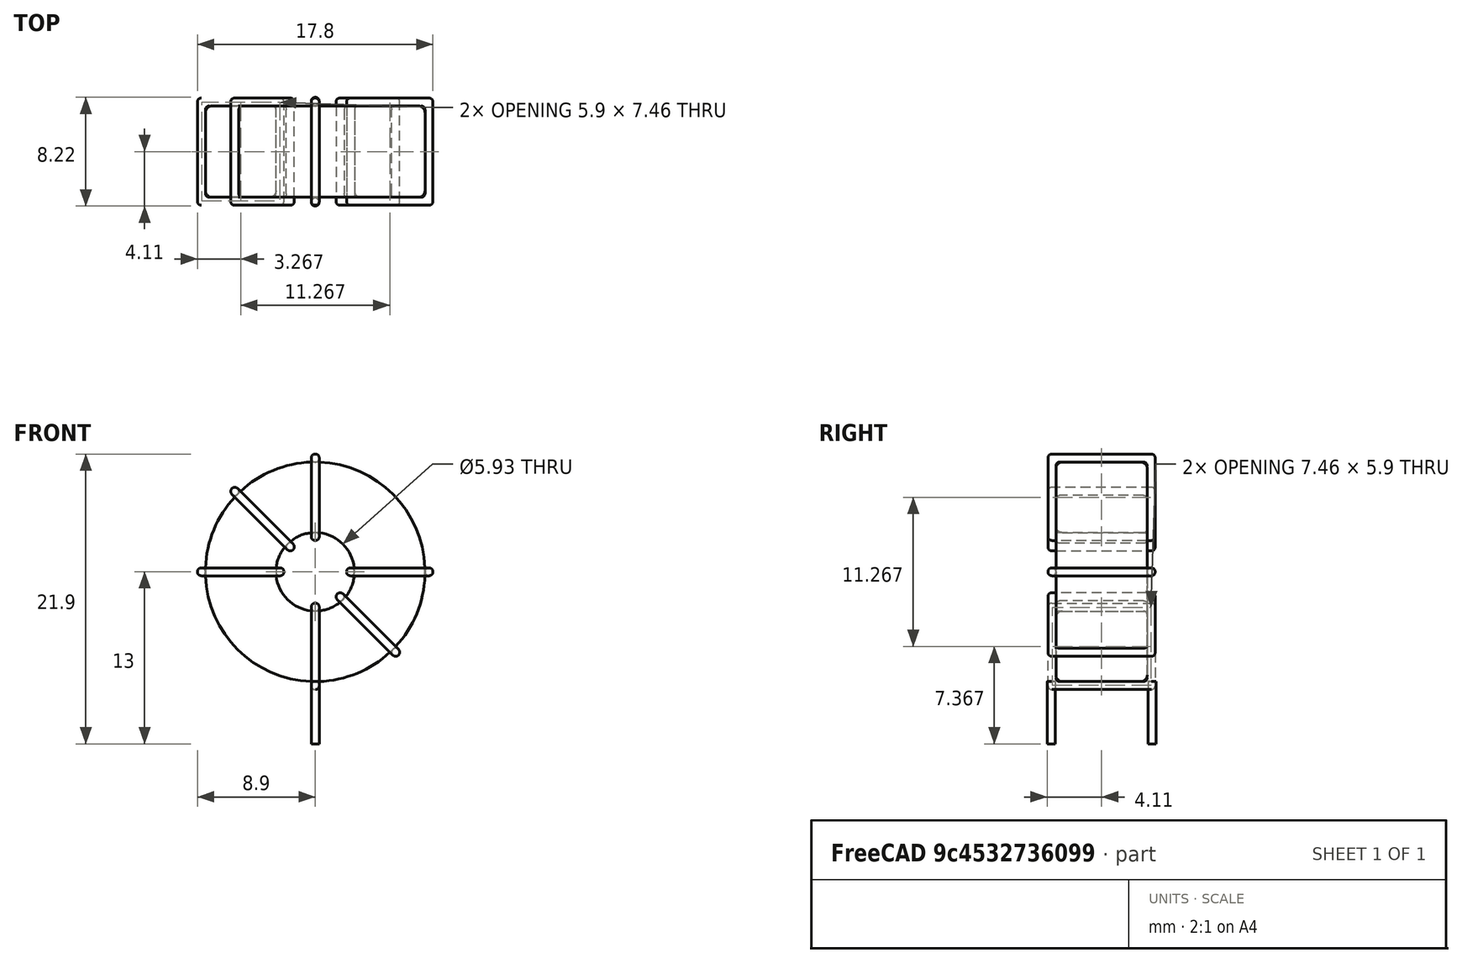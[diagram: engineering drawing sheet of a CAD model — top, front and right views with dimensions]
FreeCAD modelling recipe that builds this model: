
FCSTD DOCUMENT  (FreeCAD 0.16R6703 (Git))
Label: L_Toroid_Vertical_L17.8mm_W8.1mm_P7.62mm_Bourns_5700series
License: All rights reserved
LicenseURL: http://en.wikipedia.org/wiki/All_rights_reserved
objects: Sketcher::SketchObject×6, PartDesign::Pad×6, PartDesign::Fillet×5, Spreadsheet::Sheet×1
note: 23 computed .brp shape members not serialized (recipe doc carries the construction recipe); baked Part::Feature solids carry a one-line shape summary decoded from their .brp

FEATURE [Spreadsheet::Sheet] Spreadsheet  label="dimensions"
  cells = A1=Wx; B1(Wx)=17.8; C1(WW)=5.933333333333334; D1=17.8; A2=Wy; B2(Wy)=8.1; D2=8.1; A3=RM; B3(RMx)=7.62; C3(RMy)=0; A4=d_wire; B4(d_wire)=0.6000000000000001; A5=H; B5(H)=17.8; A6=offsetx; B6(offsetx)=8.9
FEATURE [Sketcher::SketchObject] Sketch
  Placement = pos=(0,-3.81,0) rot=(1,0,0;1.5708rad)
  expr: Placement.Base.y = -Spreadsheet.RMx / 2
  expr: Constraints[0] = Spreadsheet.Wx / 2 - Spreadsheet.d_wire
  expr: Constraints[4] = Spreadsheet.WW / 2
  expr: Constraints[2] = Spreadsheet.Wx / 2 + Spreadsheet.d_wire + 0.5
  sketch-geometry (2):
    g0: Circle CenterX=0 CenterY=10 CenterZ=0 NormalX=0 NormalY=0 NormalZ=1 Radius=8.3
    g1: Circle CenterX=0 CenterY=10 CenterZ=0 NormalX=0 NormalY=0 NormalZ=1 Radius=2.96667
  constraints (5):
    c: Radius(g0) = 8.3
    c: DistanceX(g-1,g0) = 0
    c: DistanceY(g-1,g0) = 10
    c: Coincident(g1,g0)
    c: Radius(g1) = 2.96667
FEATURE [PartDesign::Pad] Pad
  Length = 6.9
  Length2 = 100
  Midplane = true
  Placement = pos=(0,-3.81,0) rot=(1,0,0;1.5708rad)
  Sketch = -> Sketch
  Type = 0
  expr: Length = Spreadsheet.Wy - 2 * Spreadsheet.d_wire
FEATURE [Sketcher::SketchObject] Sketch001
  Placement = pos=(0,0,1.1) rot=(0,0,1;0rad)
  expr: Placement.Base.z = 0.5 + Spreadsheet.d_wire
  expr: Constraints[4] = Spreadsheet.RMy
  expr: Constraints[2] = -Spreadsheet.RMx
  expr: Constraints[1] = Spreadsheet.d_wire / 2
  sketch-geometry (2):
    g0: Circle CenterX=0 CenterY=0 CenterZ=0 NormalX=0 NormalY=0 NormalZ=1 Radius=0.3
    g1: Circle CenterX=0 CenterY=-7.62 CenterZ=0 NormalX=0 NormalY=0 NormalZ=1 Radius=0.3
  constraints (5):
    c: Equal(g0,g1)
    c: Radius(g0) = 0.3
    c: DistanceY(g-1,g1) = -7.62
    c: Coincident(g0,g-1)
    c: DistanceX(g-1,g1) = 0
FEATURE [PartDesign::Pad] Pad001
  Length = 0.6
  Length2 = 4.1
  Placement = pos=(0,0,1.1) rot=(0,0,1;0rad)
  Reversed = true
  Sketch = -> Sketch001
  Type = 4
  expr: Length2 = 3.5 + Spreadsheet.d_wire
  expr: Length = Spreadsheet.d_wire
FEATURE [PartDesign::Fillet] Fillet
  Base = -> Pad [Edge6,Edge3,Edge2]
  Placement = pos=(0,-3.81,0) rot=(1,0,0;1.5708rad)
  Radius = 0.5
FEATURE [Sketcher::SketchObject] Sketch003
  Placement = pos=(0,0.24,10) rot=(1,0,0;3.14159rad)
  expr: Constraints[18] = Spreadsheet.d_wire
  expr: Constraints[16] = Spreadsheet.d_wire
  expr: Constraints[19] = Spreadsheet.d_wire
  expr: Constraints[17] = Spreadsheet.d_wire
  expr: Placement.Base.y = -1 * (Spreadsheet.RMx - Spreadsheet.Wy) / 2
  expr: Constraints[21] = (Spreadsheet.Wx - Spreadsheet.WW) / 2 - Spreadsheet.d_wire
  expr: Constraints[22] = Spreadsheet.Wx / 2 - Spreadsheet.d_wire
  expr: Constraints[43] = Spreadsheet.d_wire
  expr: Constraints[48] = Spreadsheet.Wx - Spreadsheet.d_wire * 2
  expr: Constraints[49] = Spreadsheet.Wy
  expr: Placement.Base.z = Spreadsheet.Wx / 2 + Spreadsheet.d_wire + 0.5
  sketch-geometry (16):
    g0: LineSegment StartX=-2.36667 StartY=0 StartZ=0 EndX=-8.9 EndY=0 EndZ=0
    g1: LineSegment StartX=-8.9 StartY=0 StartZ=0 EndX=-8.9 EndY=8.1 EndZ=0
    g2: LineSegment StartX=-8.9 StartY=8.1 StartZ=0 EndX=-2.36667 EndY=8.1 EndZ=0
    g3: LineSegment StartX=-2.36667 StartY=8.1 StartZ=0 EndX=-2.36667 EndY=0 EndZ=0
    g4: LineSegment StartX=-8.3 StartY=7.5 StartZ=0 EndX=-2.96667 EndY=7.5 EndZ=0
    g5: LineSegment StartX=-2.96667 StartY=7.5 StartZ=0 EndX=-2.96667 EndY=0.6 EndZ=0
    g6: LineSegment StartX=-2.96667 StartY=0.6 StartZ=0 EndX=-8.3 EndY=0.6 EndZ=0
    g7: LineSegment StartX=-8.3 StartY=0.6 StartZ=0 EndX=-8.3 EndY=7.5 EndZ=0
    g8: LineSegment StartX=2.36667 StartY=8.1 StartZ=0 EndX=8.9 EndY=8.1 EndZ=0
    g9: LineSegment StartX=8.9 StartY=8.1 StartZ=0 EndX=8.9 EndY=0 EndZ=0
    g10: LineSegment StartX=8.9 StartY=0 StartZ=0 EndX=2.36667 EndY=0 EndZ=0
    g11: LineSegment StartX=2.36667 StartY=0 StartZ=0 EndX=2.36667 EndY=8.1 EndZ=0
    g12: LineSegment StartX=2.96667 StartY=7.5 StartZ=0 EndX=8.3 EndY=7.5 EndZ=0
    g13: LineSegment StartX=8.3 StartY=7.5 StartZ=0 EndX=8.3 EndY=0.6 EndZ=0
    g14: LineSegment StartX=8.3 StartY=0.6 StartZ=0 EndX=2.96667 EndY=0.6 EndZ=0
    g15: LineSegment StartX=2.96667 StartY=0.6 StartZ=0 EndX=2.96667 EndY=7.5 EndZ=0
  constraints (50):
    c: Horizontal(g0)
    c: Coincident(g1,g0)
    c: Vertical(g1)
    c: Coincident(g2,g1)
    c: Horizontal(g2)
    c: Coincident(g3,g2)
    c: Coincident(g3,g0)
    c: Vertical(g3)
    c: Coincident(g4,g5)
    c: Coincident(g5,g6)
    c: Coincident(g6,g7)
    c: Coincident(g7,g4)
    c: Horizontal(g4)
    c: Horizontal(g6)
    c: Vertical(g5)
    c: Vertical(g7)
    c: DistanceX(g1,g4) = 0.6
    c: DistanceY(g4,g1) = 0.6
    c: DistanceX(g5,g0) = 0.6
    c: DistanceY(g0,g5) = 0.6
    c: DistanceY(g-1,g0) = 0
    c: DistanceX(g6,g6) = 5.33333
    c: DistanceX(g6,g-1) = 8.3
    c: Coincident(g8,g9)
    c: Coincident(g9,g10)
    c: Coincident(g10,g11)
    c: Coincident(g11,g8)
    c: Horizontal(g8)
    c: Horizontal(g10)
    c: Vertical(g9)
    c: Vertical(g11)
    c: Coincident(g12,g13)
    c: Coincident(g13,g14)
    c: Coincident(g14,g15)
    c: Coincident(g15,g12)
    c: Horizontal(g12)
    c: Horizontal(g14)
    c: Vertical(g13)
    c: Vertical(g15)
    c: DistanceY(g8,g2) = 0
    c: DistanceY(g10,g0) = 0
    c: DistanceY(g14,g5) = 0
    c: DistanceY(g12,g4) = 0
    c: DistanceX(g8,g12) = 0.6
    c: Equal(g8,g2)
    c: Equal(g12,g4)
    c: Equal(g9,g1)
    c: Equal(g13,g7)
    c: DistanceX(g4,g12) = 16.6
    c: DistanceY(g0,g1) = 8.1
FEATURE [PartDesign::Pad] Pad002
  Length = 0.6
  Length2 = 100
  Midplane = true
  Placement = pos=(0,0.24,10) rot=(1,0,0;3.14159rad)
  Sketch = -> Sketch003
  Type = 0
  expr: Length = Spreadsheet.d_wire
FEATURE [PartDesign::Fillet] Fillet001
  Base = -> Pad002 [Edge38,Edge41,Edge42,Edge43,Edge29,Edge32,Edge33,Edge34,Edge25,Edge35,Edge36,Edge13,Edge14,Edge15,Edge16,Edge17,Edge18,Edge19,Edge1,Edge2,Edge3,Edge4,Edge5,Edge6,Edge7,Edge37,Edge39,Edge40,Edge20,Edge23,Edge24,Edge21,Edge22,Edge8,Edge9,Edge10,Edge11,Edge12,Edge26,Edge27,+8 more]
  Placement = pos=(0,0.24,10) rot=(1,0,0;3.14159rad)
  Radius = 0.282
  expr: Radius = Spreadsheet.d_wire * 0.47
FEATURE [Sketcher::SketchObject] Sketch004
  Placement = pos=(0,0.24,10) rot=(0.92388,0,0.382683;3.14159rad)
  expr: Constraints[18] = Spreadsheet.d_wire
  expr: Constraints[16] = Spreadsheet.d_wire
  expr: Constraints[19] = Spreadsheet.d_wire
  expr: Constraints[17] = Spreadsheet.d_wire
  expr: Placement.Base.y = -1 * (Spreadsheet.RMx - Spreadsheet.Wy) / 2
  expr: Constraints[21] = (Spreadsheet.Wx - Spreadsheet.WW) / 2 - Spreadsheet.d_wire
  expr: Constraints[22] = Spreadsheet.Wx / 2 - Spreadsheet.d_wire
  expr: Constraints[43] = Spreadsheet.d_wire
  expr: Constraints[48] = Spreadsheet.Wx - 2 * Spreadsheet.d_wire
  expr: Constraints[49] = Spreadsheet.Wy
  expr: Placement.Base.z = Spreadsheet.Wx / 2 + Spreadsheet.d_wire + 0.5
  sketch-geometry (16):
    g0: LineSegment StartX=-2.36667 StartY=0 StartZ=0 EndX=-8.9 EndY=0 EndZ=0
    g1: LineSegment StartX=-8.9 StartY=0 StartZ=0 EndX=-8.9 EndY=8.1 EndZ=0
    g2: LineSegment StartX=-8.9 StartY=8.1 StartZ=0 EndX=-2.36667 EndY=8.1 EndZ=0
    g3: LineSegment StartX=-2.36667 StartY=8.1 StartZ=0 EndX=-2.36667 EndY=0 EndZ=0
    g4: LineSegment StartX=-8.3 StartY=7.5 StartZ=0 EndX=-2.96667 EndY=7.5 EndZ=0
    g5: LineSegment StartX=-2.96667 StartY=7.5 StartZ=0 EndX=-2.96667 EndY=0.6 EndZ=0
    g6: LineSegment StartX=-2.96667 StartY=0.6 StartZ=0 EndX=-8.3 EndY=0.6 EndZ=0
    g7: LineSegment StartX=-8.3 StartY=0.6 StartZ=0 EndX=-8.3 EndY=7.5 EndZ=0
    g8: LineSegment StartX=2.36667 StartY=8.1 StartZ=0 EndX=8.9 EndY=8.1 EndZ=0
    g9: LineSegment StartX=8.9 StartY=8.1 StartZ=0 EndX=8.9 EndY=0 EndZ=0
    g10: LineSegment StartX=8.9 StartY=0 StartZ=0 EndX=2.36667 EndY=0 EndZ=0
    g11: LineSegment StartX=2.36667 StartY=0 StartZ=0 EndX=2.36667 EndY=8.1 EndZ=0
    g12: LineSegment StartX=2.96667 StartY=7.5 StartZ=0 EndX=8.3 EndY=7.5 EndZ=0
    g13: LineSegment StartX=8.3 StartY=7.5 StartZ=0 EndX=8.3 EndY=0.6 EndZ=0
    g14: LineSegment StartX=8.3 StartY=0.6 StartZ=0 EndX=2.96667 EndY=0.6 EndZ=0
    g15: LineSegment StartX=2.96667 StartY=0.6 StartZ=0 EndX=2.96667 EndY=7.5 EndZ=0
  constraints (50):
    c: Horizontal(g0)
    c: Coincident(g1,g0)
    c: Vertical(g1)
    c: Coincident(g2,g1)
    c: Horizontal(g2)
    c: Coincident(g3,g2)
    c: Coincident(g3,g0)
    c: Vertical(g3)
    c: Coincident(g4,g5)
    c: Coincident(g5,g6)
    c: Coincident(g6,g7)
    c: Coincident(g7,g4)
    c: Horizontal(g4)
    c: Horizontal(g6)
    c: Vertical(g5)
    c: Vertical(g7)
    c: DistanceX(g1,g4) = 0.6
    c: DistanceY(g4,g1) = 0.6
    c: DistanceX(g5,g0) = 0.6
    c: DistanceY(g0,g5) = 0.6
    c: DistanceY(g-1,g0) = 0
    c: DistanceX(g6,g6) = 5.33333
    c: DistanceX(g6,g-1) = 8.3
    c: Coincident(g8,g9)
    c: Coincident(g9,g10)
    c: Coincident(g10,g11)
    c: Coincident(g11,g8)
    c: Horizontal(g8)
    c: Horizontal(g10)
    c: Vertical(g9)
    c: Vertical(g11)
    c: Coincident(g12,g13)
    c: Coincident(g13,g14)
    c: Coincident(g14,g15)
    c: Coincident(g15,g12)
    c: Horizontal(g12)
    c: Horizontal(g14)
    c: Vertical(g13)
    c: Vertical(g15)
    c: DistanceY(g8,g2) = 0
    c: DistanceY(g10,g0) = 0
    c: DistanceY(g14,g5) = 0
    c: DistanceY(g12,g4) = 0
    c: DistanceX(g8,g12) = 0.6
    c: Equal(g8,g2)
    c: Equal(g12,g4)
    c: Equal(g9,g1)
    c: Equal(g13,g7)
    c: DistanceX(g4,g12) = 16.6
    c: DistanceY(g0,g1) = 8.1
FEATURE [PartDesign::Pad] Pad003
  Length = 0.6
  Length2 = 100
  Midplane = true
  Placement = pos=(0,0.24,10) rot=(0.92388,0,0.382683;3.14159rad)
  Sketch = -> Sketch004
  Type = 0
  expr: Length = Spreadsheet.d_wire
FEATURE [PartDesign::Fillet] Fillet002
  Base = -> Pad003 [Edge38,Edge41,Edge42,Edge43,Edge29,Edge32,Edge33,Edge34,Edge25,Edge35,Edge36,Edge13,Edge14,Edge15,Edge16,Edge17,Edge18,Edge19,Edge1,Edge2,Edge3,Edge4,Edge5,Edge6,Edge7,Edge37,Edge39,Edge40,Edge20,Edge23,Edge24,Edge21,Edge22,Edge8,Edge9,Edge10,Edge11,Edge12,Edge26,Edge27,+8 more]
  Placement = pos=(0,0.24,10) rot=(0.92388,0,0.382683;3.14159rad)
  Radius = 0.282
  expr: Radius = Spreadsheet.d_wire * 0.47
FEATURE [Sketcher::SketchObject] Sketch005
  Placement = pos=(0,0.24,10) rot=(0.92388,0,-0.382683;3.14159rad)
  expr: Constraints[18] = Spreadsheet.d_wire
  expr: Constraints[16] = Spreadsheet.d_wire
  expr: Constraints[19] = Spreadsheet.d_wire
  expr: Constraints[17] = Spreadsheet.d_wire
  expr: Placement.Base.y = -1 * (Spreadsheet.RMx - Spreadsheet.Wy) / 2
  expr: Constraints[21] = (Spreadsheet.Wx - Spreadsheet.WW) / 2 - Spreadsheet.d_wire
  expr: Constraints[22] = Spreadsheet.Wx / 2 - Spreadsheet.d_wire
  expr: Constraints[43] = Spreadsheet.d_wire
  expr: Constraints[48] = Spreadsheet.Wx - 2 * Spreadsheet.d_wire
  expr: Constraints[49] = Spreadsheet.Wy
  expr: Placement.Base.z = Spreadsheet.Wx / 2 + Spreadsheet.d_wire + 0.5
  sketch-geometry (16):
    g0: LineSegment StartX=-2.36667 StartY=0 StartZ=0 EndX=-8.9 EndY=0 EndZ=0
    g1: LineSegment StartX=-8.9 StartY=0 StartZ=0 EndX=-8.9 EndY=8.1 EndZ=0
    g2: LineSegment StartX=-8.9 StartY=8.1 StartZ=0 EndX=-2.36667 EndY=8.1 EndZ=0
    g3: LineSegment StartX=-2.36667 StartY=8.1 StartZ=0 EndX=-2.36667 EndY=0 EndZ=0
    g4: LineSegment StartX=-8.3 StartY=7.5 StartZ=0 EndX=-2.96667 EndY=7.5 EndZ=0
    g5: LineSegment StartX=-2.96667 StartY=7.5 StartZ=0 EndX=-2.96667 EndY=0.6 EndZ=0
    g6: LineSegment StartX=-2.96667 StartY=0.6 StartZ=0 EndX=-8.3 EndY=0.6 EndZ=0
    g7: LineSegment StartX=-8.3 StartY=0.6 StartZ=0 EndX=-8.3 EndY=7.5 EndZ=0
    g8: LineSegment StartX=2.36667 StartY=8.1 StartZ=0 EndX=8.9 EndY=8.1 EndZ=0
    g9: LineSegment StartX=8.9 StartY=8.1 StartZ=0 EndX=8.9 EndY=0 EndZ=0
    g10: LineSegment StartX=8.9 StartY=0 StartZ=0 EndX=2.36667 EndY=0 EndZ=0
    g11: LineSegment StartX=2.36667 StartY=0 StartZ=0 EndX=2.36667 EndY=8.1 EndZ=0
    g12: LineSegment StartX=2.96667 StartY=7.5 StartZ=0 EndX=8.3 EndY=7.5 EndZ=0
    g13: LineSegment StartX=8.3 StartY=7.5 StartZ=0 EndX=8.3 EndY=0.6 EndZ=0
    g14: LineSegment StartX=8.3 StartY=0.6 StartZ=0 EndX=2.96667 EndY=0.6 EndZ=0
    g15: LineSegment StartX=2.96667 StartY=0.6 StartZ=0 EndX=2.96667 EndY=7.5 EndZ=0
  constraints (50):
    c: Horizontal(g0)
    c: Coincident(g1,g0)
    c: Vertical(g1)
    c: Coincident(g2,g1)
    c: Horizontal(g2)
    c: Coincident(g3,g2)
    c: Coincident(g3,g0)
    c: Vertical(g3)
    c: Coincident(g4,g5)
    c: Coincident(g5,g6)
    c: Coincident(g6,g7)
    c: Coincident(g7,g4)
    c: Horizontal(g4)
    c: Horizontal(g6)
    c: Vertical(g5)
    c: Vertical(g7)
    c: DistanceX(g1,g4) = 0.6
    c: DistanceY(g4,g1) = 0.6
    c: DistanceX(g5,g0) = 0.6
    c: DistanceY(g0,g5) = 0.6
    c: DistanceY(g-1,g0) = 0
    c: DistanceX(g6,g6) = 5.33333
    c: DistanceX(g6,g-1) = 8.3
    c: Coincident(g8,g9)
    c: Coincident(g9,g10)
    c: Coincident(g10,g11)
    c: Coincident(g11,g8)
    c: Horizontal(g8)
    c: Horizontal(g10)
    c: Vertical(g9)
    c: Vertical(g11)
    c: Coincident(g12,g13)
    c: Coincident(g13,g14)
    c: Coincident(g14,g15)
    c: Coincident(g15,g12)
    c: Horizontal(g12)
    c: Horizontal(g14)
    c: Vertical(g13)
    c: Vertical(g15)
    c: DistanceY(g8,g2) = 0
    c: DistanceY(g10,g0) = 0
    c: DistanceY(g14,g5) = 0
    c: DistanceY(g12,g4) = 0
    c: DistanceX(g8,g12) = 0.6
    c: Equal(g8,g2)
    c: Equal(g12,g4)
    c: Equal(g9,g1)
    c: Equal(g13,g7)
    c: DistanceX(g4,g12) = 16.6
    c: DistanceY(g0,g1) = 8.1
FEATURE [PartDesign::Pad] Pad004
  Length = 0.6
  Length2 = 100
  Midplane = true
  Placement = pos=(0,0.24,10) rot=(0.92388,0,-0.382683;3.14159rad)
  Sketch = -> Sketch005
  Type = 0
  expr: Length = Spreadsheet.d_wire
FEATURE [PartDesign::Fillet] Fillet003
  Base = -> Pad004 [Edge38,Edge41,Edge42,Edge43,Edge29,Edge32,Edge33,Edge34,Edge25,Edge35,Edge36,Edge13,Edge14,Edge15,Edge16,Edge17,Edge18,Edge19,Edge1,Edge2,Edge3,Edge4,Edge5,Edge6,Edge7,Edge37,Edge39,Edge40,Edge20,Edge23,Edge24,Edge21,Edge22,Edge8,Edge9,Edge10,Edge11,Edge12,Edge26,Edge27,+8 more]
  Placement = pos=(0,0.24,10) rot=(0.92388,0,-0.382683;3.14159rad)
  Radius = 0.282
  expr: Radius = Spreadsheet.d_wire * 0.47
FEATURE [Sketcher::SketchObject] Sketch006
  Placement = pos=(0,0.24,10) rot=(0.707107,0,0.707107;3.14159rad)
  expr: Constraints[18] = Spreadsheet.d_wire
  expr: Constraints[16] = Spreadsheet.d_wire
  expr: Constraints[19] = Spreadsheet.d_wire
  expr: Constraints[17] = Spreadsheet.d_wire
  expr: Placement.Base.y = -1 * (Spreadsheet.RMx - Spreadsheet.Wy) / 2
  expr: Constraints[21] = (Spreadsheet.Wx - Spreadsheet.WW) / 2 - Spreadsheet.d_wire
  expr: Constraints[22] = Spreadsheet.Wx / 2 - Spreadsheet.d_wire
  expr: Constraints[43] = Spreadsheet.d_wire
  expr: Constraints[48] = Spreadsheet.Wx - Spreadsheet.d_wire * 2
  expr: Constraints[49] = Spreadsheet.Wy
  expr: Placement.Base.z = Spreadsheet.Wx / 2 + Spreadsheet.d_wire + 0.5
  sketch-geometry (16):
    g0: LineSegment StartX=-2.36667 StartY=0 StartZ=0 EndX=-8.9 EndY=0 EndZ=0
    g1: LineSegment StartX=-8.9 StartY=0 StartZ=0 EndX=-8.9 EndY=8.1 EndZ=0
    g2: LineSegment StartX=-8.9 StartY=8.1 StartZ=0 EndX=-2.36667 EndY=8.1 EndZ=0
    g3: LineSegment StartX=-2.36667 StartY=8.1 StartZ=0 EndX=-2.36667 EndY=0 EndZ=0
    g4: LineSegment StartX=-8.3 StartY=7.5 StartZ=0 EndX=-2.96667 EndY=7.5 EndZ=0
    g5: LineSegment StartX=-2.96667 StartY=7.5 StartZ=0 EndX=-2.96667 EndY=0.6 EndZ=0
    g6: LineSegment StartX=-2.96667 StartY=0.6 StartZ=0 EndX=-8.3 EndY=0.6 EndZ=0
    g7: LineSegment StartX=-8.3 StartY=0.6 StartZ=0 EndX=-8.3 EndY=7.5 EndZ=0
    g8: LineSegment StartX=2.36667 StartY=8.1 StartZ=0 EndX=8.9 EndY=8.1 EndZ=0
    g9: LineSegment StartX=8.9 StartY=8.1 StartZ=0 EndX=8.9 EndY=0 EndZ=0
    g10: LineSegment StartX=8.9 StartY=0 StartZ=0 EndX=2.36667 EndY=0 EndZ=0
    g11: LineSegment StartX=2.36667 StartY=0 StartZ=0 EndX=2.36667 EndY=8.1 EndZ=0
    g12: LineSegment StartX=2.96667 StartY=7.5 StartZ=0 EndX=8.3 EndY=7.5 EndZ=0
    g13: LineSegment StartX=8.3 StartY=7.5 StartZ=0 EndX=8.3 EndY=0.6 EndZ=0
    g14: LineSegment StartX=8.3 StartY=0.6 StartZ=0 EndX=2.96667 EndY=0.6 EndZ=0
    g15: LineSegment StartX=2.96667 StartY=0.6 StartZ=0 EndX=2.96667 EndY=7.5 EndZ=0
  constraints (50):
    c: Horizontal(g0)
    c: Coincident(g1,g0)
    c: Vertical(g1)
    c: Coincident(g2,g1)
    c: Horizontal(g2)
    c: Coincident(g3,g2)
    c: Coincident(g3,g0)
    c: Vertical(g3)
    c: Coincident(g4,g5)
    c: Coincident(g5,g6)
    c: Coincident(g6,g7)
    c: Coincident(g7,g4)
    c: Horizontal(g4)
    c: Horizontal(g6)
    c: Vertical(g5)
    c: Vertical(g7)
    c: DistanceX(g1,g4) = 0.6
    c: DistanceY(g4,g1) = 0.6
    c: DistanceX(g5,g0) = 0.6
    c: DistanceY(g0,g5) = 0.6
    c: DistanceY(g-1,g0) = 0
    c: DistanceX(g6,g6) = 5.33333
    c: DistanceX(g6,g-1) = 8.3
    c: Coincident(g8,g9)
    c: Coincident(g9,g10)
    c: Coincident(g10,g11)
    c: Coincident(g11,g8)
    c: Horizontal(g8)
    c: Horizontal(g10)
    c: Vertical(g9)
    c: Vertical(g11)
    c: Coincident(g12,g13)
    c: Coincident(g13,g14)
    c: Coincident(g14,g15)
    c: Coincident(g15,g12)
    c: Horizontal(g12)
    c: Horizontal(g14)
    c: Vertical(g13)
    c: Vertical(g15)
    c: DistanceY(g8,g2) = 0
    c: DistanceY(g10,g0) = 0
    c: DistanceY(g14,g5) = 0
    c: DistanceY(g12,g4) = 0
    c: DistanceX(g8,g12) = 0.6
    c: Equal(g8,g2)
    c: Equal(g12,g4)
    c: Equal(g9,g1)
    c: Equal(g13,g7)
    c: DistanceX(g4,g12) = 16.6
    c: DistanceY(g0,g1) = 8.1
FEATURE [PartDesign::Pad] Pad005
  Length = 0.6
  Length2 = 100
  Midplane = true
  Placement = pos=(0,0.24,10) rot=(0.707107,0,0.707107;3.14159rad)
  Sketch = -> Sketch006
  Type = 0
  expr: Length = Spreadsheet.d_wire
FEATURE [PartDesign::Fillet] Fillet004
  Base = -> Pad005 [Edge38,Edge41,Edge42,Edge43,Edge29,Edge32,Edge33,Edge34,Edge25,Edge35,Edge36,Edge13,Edge14,Edge15,Edge16,Edge17,Edge18,Edge19,Edge1,Edge2,Edge3,Edge4,Edge5,Edge6,Edge7,Edge37,Edge39,Edge40,Edge20,Edge23,Edge24,Edge21,Edge22,Edge8,Edge9,Edge10,Edge11,Edge12,Edge26,Edge27,+8 more]
  Placement = pos=(0,0.24,10) rot=(0.707107,0,0.707107;3.14159rad)
  Radius = 0.282
  expr: Radius = Spreadsheet.d_wire * 0.47
